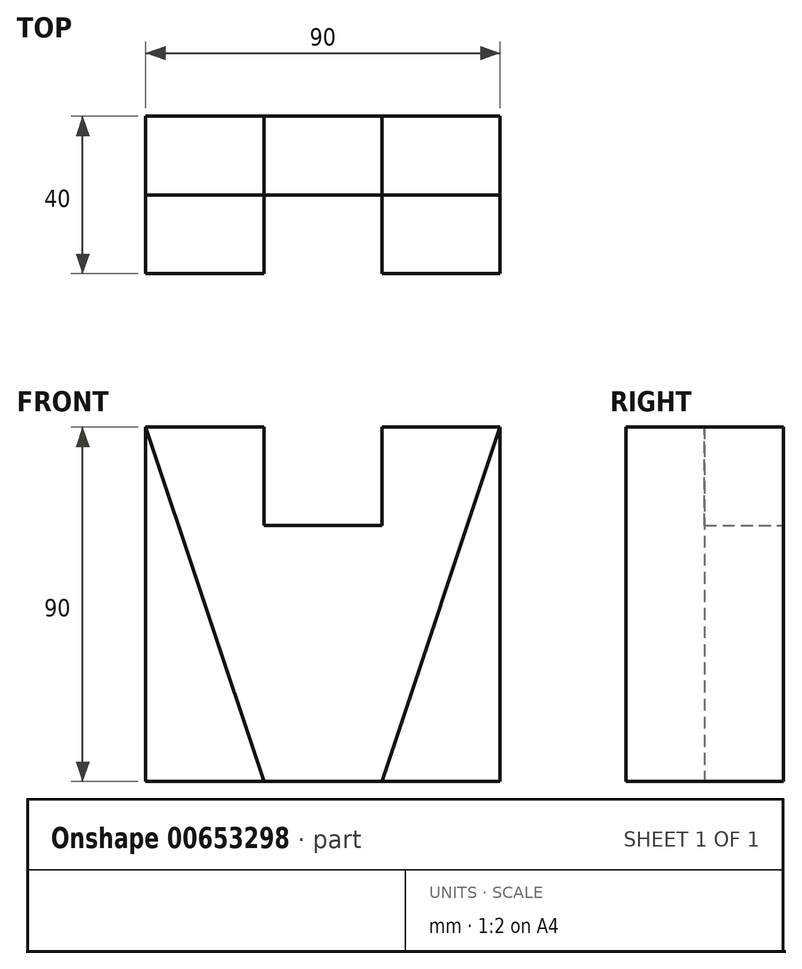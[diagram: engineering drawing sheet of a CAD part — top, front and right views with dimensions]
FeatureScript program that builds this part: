
annotation { "Feature Type Name" : "Feature", "Feature Type Description" : "" }
export const myFeature = defineFeature(function(context is Context, id is Id, definition is map)
    precondition{}
    {
        {
            var Q0;
            Q0=qCreatedBy(makeId("Front.planeOp"),FACE);
            var sketch = newSketch(context, id + "F0", { "sketchPlane" : qUnion([Q0])});
            skLineSegment(sketch, "E0.bottom", {"start": v(-15, 32.5) * mm, "end": v(15, 32.5) * mm});
            skLineSegment(sketch, "E0.top", {"start": v(-45, -32.5) * mm, "end": v(45, -32.5) * mm});
            skLineSegment(sketch, "E0.left", {"start": v(-45, 32.5) * mm, "end": v(-45, -32.5) * mm});
            skLineSegment(sketch, "E0.right", {"start": v(45, 32.5) * mm, "end": v(45, -32.5) * mm});
            skPoint(sketch, "E0.middle", {"position": v(0, 0) * mm});
            skLineSegment(sketch, "E1.top", {"start": v(-45, 57.5) * mm, "end": v(-15, 57.5) * mm});
            skLineSegment(sketch, "E1.left", {"start": v(-45, 32.5) * mm, "end": v(-45, 57.5) * mm});
            skLineSegment(sketch, "E1.right", {"start": v(-15, 32.5) * mm, "end": v(-15, 57.5) * mm});
            skLineSegment(sketch, "E2.right", {"start": v(15, 32.5) * mm, "end": v(15, 57.5) * mm});
            skLineSegment(sketch, "E3.top", {"start": v(15, 57.5) * mm, "end": v(45, 57.5) * mm});
            skLineSegment(sketch, "E3.right", {"start": v(45, 32.5) * mm, "end": v(45, 57.5) * mm});
            skSolve(sketch);
        }
        {
            var Q0;
            Q0=makeQuery(id+"F0.imprint","IMPRINT",FACE,{"disambiguationData":[TD([[makeQuery(id+"F0.imprint","IMPRINT",EDGE,{"derivedFrom":sQuery(id+"F0.wireOp",EDGE,"E0.top")}),1.0]])]});
            extrude(context, id + "F1", {"entities" : qUnion([Q0]), "depth" : 20 * mm, "offsetDistance" : 25 * mm});
        }
        {
            var Q0;
            Q0=makeQuery(id+"F1.opExtrude","CAP_FACE",FACE,{"disambiguationData":[OSD([sQuery(id+"F0.wireOp",EDGE,"E0.top"),sQuery(id+"F0.wireOp",EDGE,"E0.left"),sQuery(id+"F0.wireOp",EDGE,"E0.right"),sQuery(id+"F0.wireOp",EDGE,"E1.top"),sQuery(id+"F0.wireOp",EDGE,"E1.left"),sQuery(id+"F0.wireOp",EDGE,"E0.bottom"),sQuery(id+"F0.wireOp",EDGE,"E1.right"),sQuery(id+"F0.wireOp",EDGE,"E3.top"),sQuery(id+"F0.wireOp",EDGE,"E2.right"),sQuery(id+"F0.wireOp",EDGE,"E3.right")])],"isStart":false});
            var sketch = newSketch(context, id + "F2", { "sketchPlane" : qUnion([Q0])});
            skLineSegment(sketch, "E4", {"start": v(-45, 57.5) * mm, "end": v(-15, -32.5) * mm});
            skLineSegment(sketch, "E5", {"start": v(45, 57.5) * mm, "end": v(15, -32.5) * mm});
            skSolve(sketch);
        }
        {
            var Q0;
            {var subQ0=sQuery(id+"F2.wireOp",EDGE,"E4");Q0=makeQuery(id+"F2.imprint","IMPRINT",FACE,{"disambiguationData":[TD([[makeQuery(id+"F2.imprint","IMPRINT",EDGE,{"derivedFrom":subQ0}),-1.0]])]});}
            var Q1;
            {var subQ0=sQuery(id+"F2.wireOp",EDGE,"E5");Q1=makeQuery(id+"F2.imprint","IMPRINT",FACE,{"disambiguationData":[TD([[makeQuery(id+"F2.imprint","IMPRINT",EDGE,{"derivedFrom":subQ0}),1.0]])]});}
            extrude(context, id + "F3", {"entities" : qUnion([Q0, Q1]), "operationType" : NewBodyOperationType.ADD, "depth" : 20 * mm, "offsetDistance" : 25 * mm});
        }
    });
